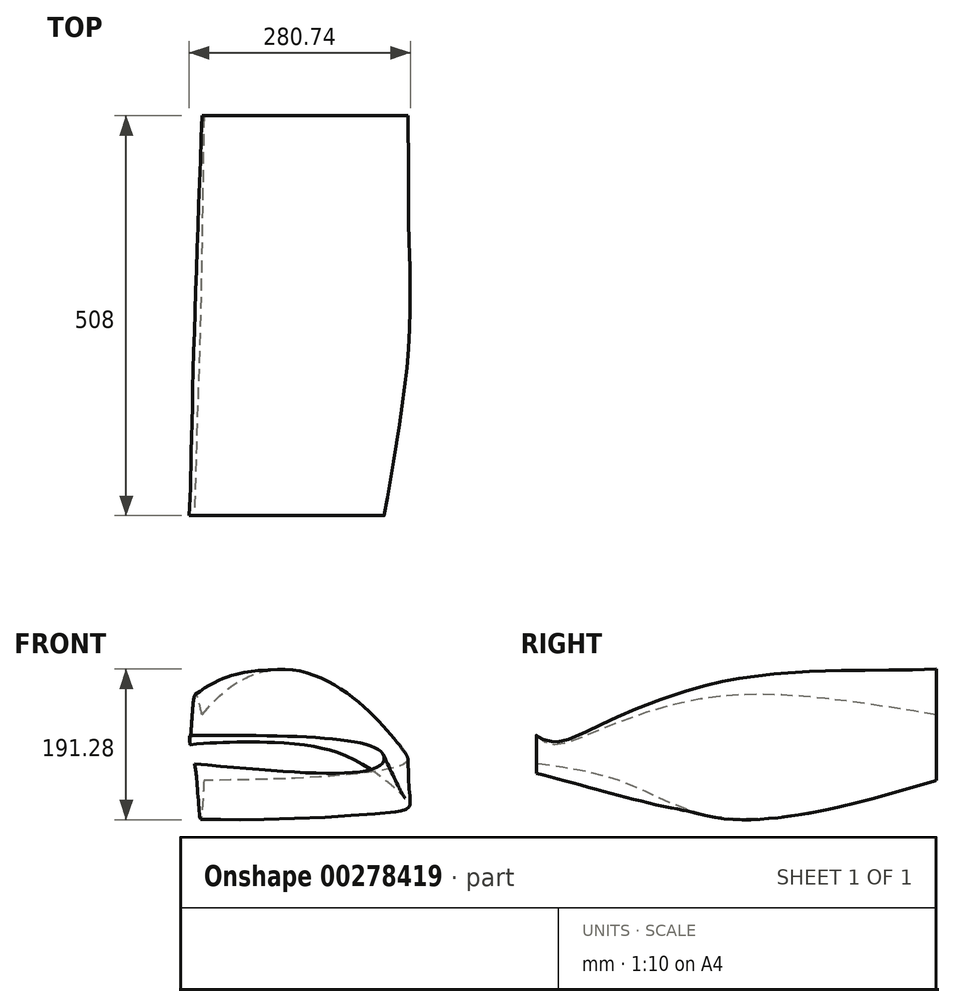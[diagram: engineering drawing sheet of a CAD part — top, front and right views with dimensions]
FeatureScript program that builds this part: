
annotation { "Feature Type Name" : "Feature", "Feature Type Description" : "" }
export const myFeature = defineFeature(function(context is Context, id is Id, definition is map)
    precondition{}
    {
        {
            var Q0;
            Q0=qCreatedBy(makeId("Front.planeOp"),FACE);
            var sketch = newSketch(context, id + "F0", { "sketchPlane" : qUnion([Q0])});
            skFitSpline(sketch, "E0", {"points": [v(-123.01, 46.84) * mm, v(128.18, 7.68) * mm, v(135.33, -14.54) * mm, v(-120.75, -36.39) * mm], "startDerivative": vector(737.44, 912.75) * mm, "endDerivative": vector(-814.37, -0.18) * mm});
            skSolve(sketch);
        }
        {
            var Q0;
            Q0=qCreatedBy(makeId("Front.planeOp"),FACE);
            cPlane(context, id + "F1", {"entities" : qUnion([Q0]), "cplaneType" : CPlaneType.OFFSET, "offset" : 508 * mm, "width" : 152.4 * mm, "height" : 152.4 * mm});
        }
        {
            var Q0;
            Q0=qCreatedBy(id+"F1.planeOp",FACE);
            var sketch = newSketch(context, id + "F2", { "sketchPlane" : qUnion([Q0])});
            skFitSpline(sketch, "E1", {"points": [v(-139.24, 20.83) * mm, v(104.16, 0) * mm, v(103.06, -17.54) * mm, v(-132.66, -15.35) * mm], "startDerivative": vector(747.2, -0.38) * mm, "endDerivative": vector(-727.54, 69.7) * mm});
            skSolve(sketch);
        }
        {
            var Q0;
            Q0=sQuery(id+"F0.wireOp",VERTEX,"E0.start");
            var Q1;
            Q1=sQuery(id+"F2.wireOp",VERTEX,"E1.start");
            var Q2;
            Q2=sQuery(id+"F0.wireOp",VERTEX,"E0.3.internal");
            cPlane(context, id + "F3", {"entities" : qUnion([Q0, Q1, Q2]), "cplaneType" : CPlaneType.THREE_POINT, "offset" : 25.4 * mm, "width" : 152.4 * mm, "height" : 152.4 * mm});
        }
        {
            var Q0;
            Q0=qCreatedBy(id+"F3.planeOp",FACE);
            var sketch = newSketch(context, id + "F4", { "sketchPlane" : qUnion([Q0])});
            skFitSpline(sketch, "E2", {"points": [v(4.05, 50.16) * mm, v(284.09, 73.15) * mm, v(452.56, 22.7) * mm, v(512.34, 24.6) * mm], "startDerivative": vector(649.9, 104.96) * mm, "endDerivative": vector(255.23, 285.79) * mm});
            skSolve(sketch);
        }
        {
            var Q0;
            Q0=sQuery(id+"F2.wireOp",VERTEX,"E1.1.internal");
            var Q1;
            Q1=sQuery(id+"F0.wireOp",VERTEX,"E0.1.internal");
            var Q2;
            Q2=sQuery(id+"F0.wireOp",VERTEX,"E0.2.internal");
            cPlane(context, id + "F5", {"entities" : qUnion([Q0, Q1, Q2]), "cplaneType" : CPlaneType.THREE_POINT, "offset" : 25.4 * mm, "width" : 152.4 * mm, "height" : 152.4 * mm});
        }
        {
            var Q0;
            Q0=qCreatedBy(id+"F5.planeOp",FACE);
            var sketch = newSketch(context, id + "F6", { "sketchPlane" : qUnion([Q0])});
            skFitSpline(sketch, "E3", {"points": [v(-502.46, -31.93) * mm, v(-276.46, -96.71) * mm, v(-133.02, -65.98) * mm, v(6.17, -31.98) * mm], "startDerivative": vector(605, -248.6) * mm, "endDerivative": vector(488.78, 143.32) * mm});
            skSolve(sketch);
        }
        {
            var Q0;
            Q0=sQuery(id+"F0.wireOp",VERTEX,"E0.3.internal");
            var Q1;
            Q1=sQuery(id+"F2.wireOp",VERTEX,"E1.3.internal");
            var Q2;
            Q2=sQuery(id+"F0.wireOp",VERTEX,"E0.0.internal");
            cPlane(context, id + "F7", {"entities" : qUnion([Q0, Q1, Q2]), "cplaneType" : CPlaneType.THREE_POINT, "offset" : 25.4 * mm, "width" : 152.4 * mm, "height" : 152.4 * mm});
        }
        {
            var Q0;
            Q0=qCreatedBy(id+"F7.planeOp",FACE);
            var sketch = newSketch(context, id + "F8", { "sketchPlane" : qUnion([Q0])});
            skFitSpline(sketch, "E4", {"points": [v(-2.72, -33.1) * mm, v(-275.77, -80.48) * mm, v(-400.4, -35.17) * mm, v(-510.84, -11.74) * mm], "startDerivative": vector(-674.16, -204.1) * mm, "endDerivative": vector(-380.02, 51.99) * mm});
            skSolve(sketch);
        }
        {
            var Q0;
            Q0=sQuery(id+"F0.wireOp",EDGE,"E0");
            var Q1;
            Q1=sQuery(id+"F2.wireOp",EDGE,"E1");
            var Q2;
            Q2=sQuery(id+"F6.wireOp",EDGE,"E3");
            var Q3;
            Q3=sQuery(id+"F8.wireOp",EDGE,"E4");
            var Q4;
            Q4=sQuery(id+"F4.wireOp",EDGE,"E2");
            loft(context, id + "F9", {"bodyType" : ToolBodyType.SURFACE, "addGuides" : true, "wireProfilesArray" : [{ "wireProfileEntities" : qUnion([Q0]) }, { "wireProfileEntities" : qUnion([Q1]) }], "guidesArray" : [{ "guideEntities" : qUnion([Q2]), "guideDerivativeType" : LoftGuideDerivativeType.DEFAULT, "guideDerivativeMagnitude" : 1 }, { "guideEntities" : qUnion([Q3]), "guideDerivativeType" : LoftGuideDerivativeType.DEFAULT, "guideDerivativeMagnitude" : 1 }, { "guideEntities" : qUnion([Q4]), "guideDerivativeType" : LoftGuideDerivativeType.DEFAULT, "guideDerivativeMagnitude" : 1 }]});
        }
    });
